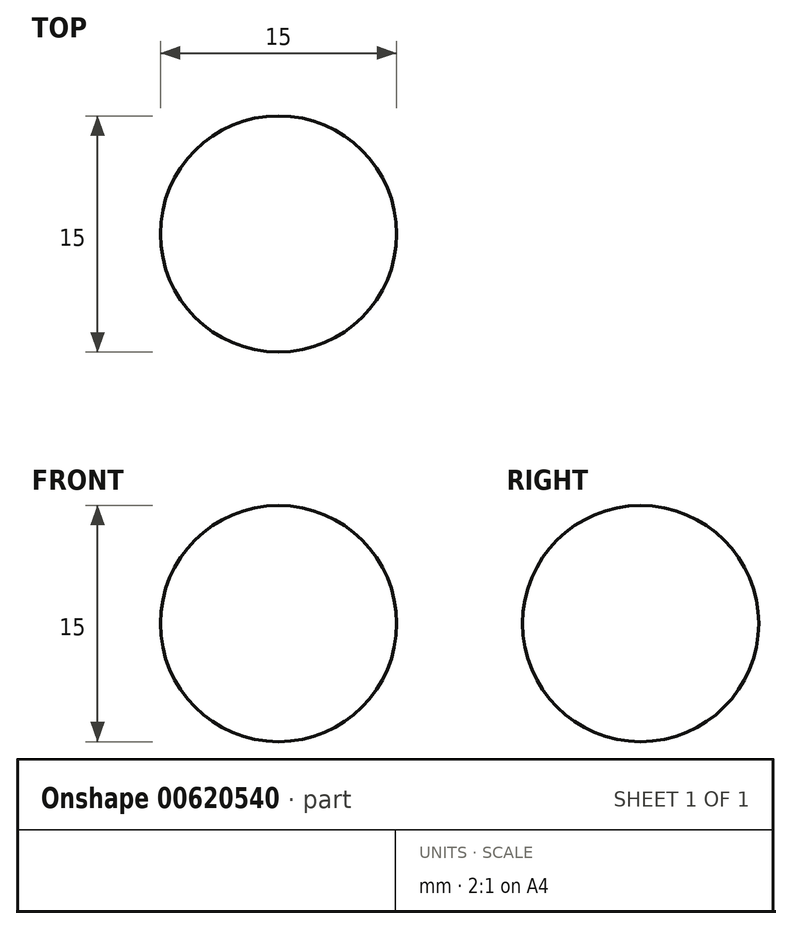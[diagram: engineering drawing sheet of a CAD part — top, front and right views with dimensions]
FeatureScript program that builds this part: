
annotation { "Feature Type Name" : "Feature", "Feature Type Description" : "" }
export const myFeature = defineFeature(function(context is Context, id is Id, definition is map)
    precondition{}
    {
        {
            var Q0;
            Q0=qCreatedBy(makeId("Top.planeOp"),FACE);
            var sketch = newSketch(context, id + "F0", { "sketchPlane" : qUnion([Q0])});
            skArc(sketch, "E0", {"start": v(0, 7.5) * mm, "mid": v(-7.5, 0) * mm, "end": v(0, -7.5) * mm});
            skLineSegment(sketch, "E1", {"start": v(0, 7.5) * mm, "end": v(0, -7.5) * mm});
            skSolve(sketch);
        }
        {
            var Q0;
            Q0 = qSketchRegion(id + "F0", true);
            var Q1;
            Q1=sQuery(id+"F0.wireOp",EDGE,"E1");
            revolve(context, id + "F1", {"surfaceOperationType" : NewSurfaceOperationType.NEW, "entities" : qUnion([Q0]), "axis" : qUnion([Q1]), "revolveType" : RevolveType.FULL});
        }
    });
